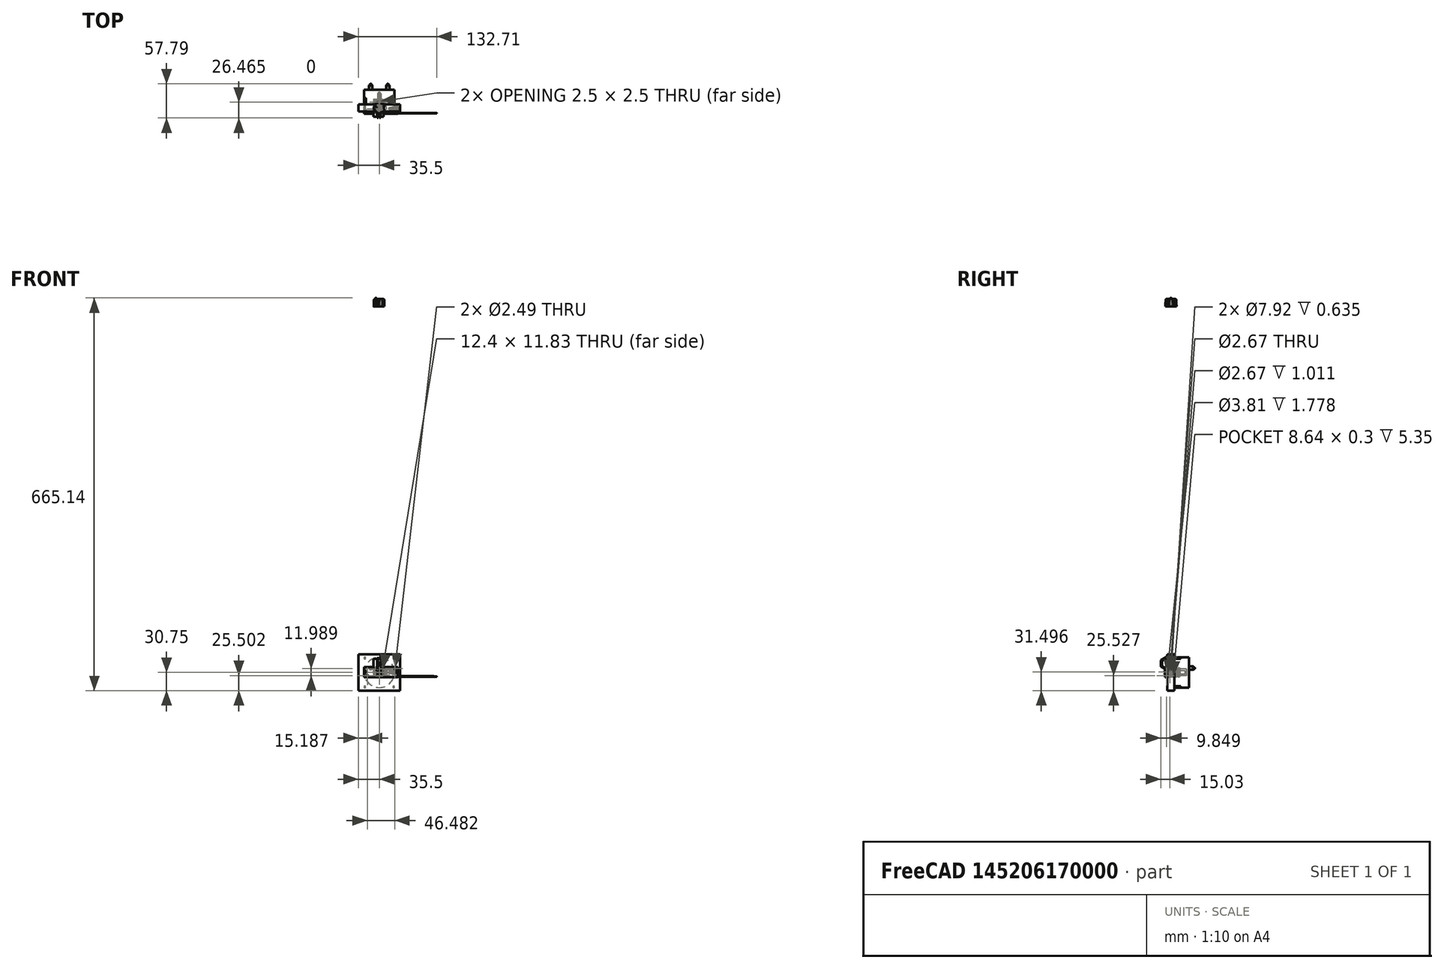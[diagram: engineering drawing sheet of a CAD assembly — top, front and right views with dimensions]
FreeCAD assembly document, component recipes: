
FREECAD ASSEMBLY — COMPONENT RECIPES ("console-placement")

This assembly document has 5 components, labeled P0..P4 below (a component is one placed body or linked part). 0 of them carry a construction recipe — the FreeCAD feature program that regenerates the part from scratch, quoted from this document or its linked companion documents; the rest are supplied as boundary geometry only. No exploded tour is included for this assembly.
COMPONENT P0 — geometry summary ("300DP6R7BLKM3QEBLK004"; no construction recipe available for this part):
  bounding box: 36.8 x 19.9 x 15.8 mm
  tessellated surface: 6,868 triangles
  volume: 3188 mm^3 (28% of its bounding box)
  symmetry: 2-fold rotationally symmetric about the x axis; mirror-symmetric across its y mid-plane, z mid-plane
COMPONENT P1 — geometry summary ("1M-pot001"; no construction recipe available for this part):
  bounding box: 24.8 x 24.5 x 16.5 mm
  tessellated surface: 1,784 triangles
  volume: 2486 mm^3 (25% of its bounding box)
  symmetry: mirror-symmetric across its z mid-plane
COMPONENT P2 — geometry summary ("knob001"; no construction recipe available for this part):
  bounding box: 18.9 x 18.1 x 14.6 mm
  tessellated surface: 16,840 triangles
  volume: 2396 mm^3 (48% of its bounding box)
  symmetry: mirror-symmetric across its y mid-plane
COMPONENT P3 — geometry summary ("meter001"; no construction recipe available for this part):
  bounding box: 71.0 x 61.5 x 46.7 mm
  tessellated surface: 35,058 triangles
  volume: 103142 mm^3 (51% of its bounding box)
  symmetry: mirror-symmetric across its y mid-plane
COMPONENT P4 — geometry summary ("meter002"; no construction recipe available for this part):
  bounding box: 71.0 x 61.5 x 46.7 mm
  tessellated surface: 35,058 triangles
  volume: 103142 mm^3 (51% of its bounding box)
  symmetry: mirror-symmetric across its y mid-plane
PROVENANCE & LICENSES
A FreeCAD (.FCStd) document from a public repository crawl; recipes are the document's own serialized feature recipes (and, for linked parts, companion documents' recipes).
License: mit.
